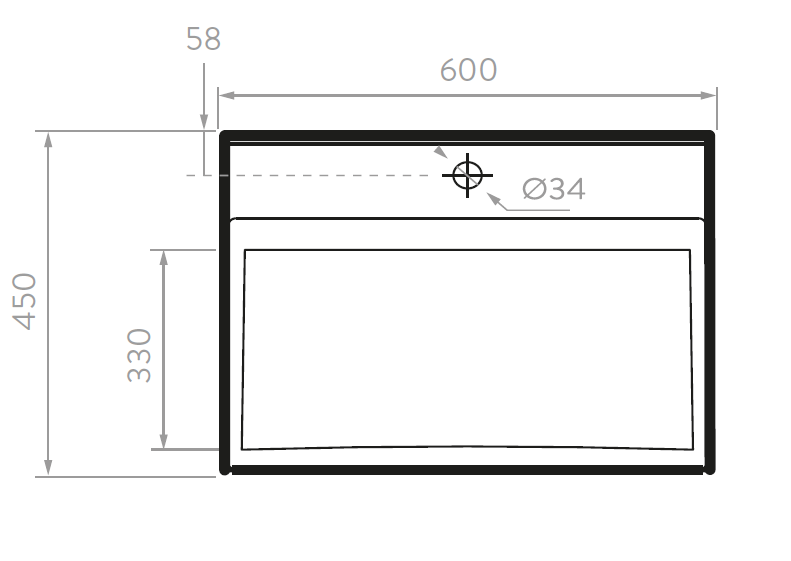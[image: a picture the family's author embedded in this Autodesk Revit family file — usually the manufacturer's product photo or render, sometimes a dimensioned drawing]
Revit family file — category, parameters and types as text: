
# Revit family: LM0066101_Mueble Fussion Vital
name_source: partatom
category: Modelos genéricos
units: mm (PartAtom-declared; Revit-internal decimal feet)

## family parameters
Anfitrión = Muro
Compartido = No
Corte con vacíos al cargar = No
Cota de conector redondo = Diámetro de uso
Número OmniClass = 23.31.13.11
Puede alojar armadura = No
Punto de cálculo de habitación = No
Siempre vertical = Sí
Tipo de pieza = Normal
Título OmniClass = Single Sinks

## types (1)
- Ref. LM0066101 Mueble Fussion Vital
    Alto = 450 mm  [stored 1.47638 ft]
    Ancho = 600 mm  [stored 1.9685 ft]
    Canto = PVC rígido 22 mm de calibre.
    Creado por = IDD
    Densidad = 15mm 670 kg./m^3.
    Descripción = Línea de Muebles Fussion Vital con cortes diagonales que brindan diseño de
vanguardia para tu baño.
· Repisas visibles para almacenamiento de fácil acceso.
· Máxima capacidad de almacenamiento.
· Lavamanos 100% en porcelana
· Resistentes a la humedad.
    Dimensiones Generales (H*W*P) = 17,72” x 23,62” x 17,56” (450,0 x 600 x 446 mm).
    Fabricante = Corona
    Fecha de creación = 21/07/2020
    Garantia Madera = 5 años
    Garantía Herrajes = 1 año
    Material = Corona_Madera_Aglomerada_Plomo
    Material puertas = Corona_Madera_Aglomerada_Duna
    Peso Bruto aprox = 30,4 lb (13,8 kg).
    Peso Neto aprox = 28,7 lb (13 kg).
    Profundidad = 446 mm
    Resistencia a la humedad = 8%.
    Resistencia al rayado = 700 ciclos.
    Textura = Duna: Poro.
Plomo: Mate.
    URL = https://corona.co

note: [stored X ft] marks values corroborated as IEEE doubles in the binary element streams (Revit-internal decimal feet)

## geometry (parser evidence)
native form markers: Blend x3, Extrusion x1, Sweep x7
no freeform markers — native parametric forms only
